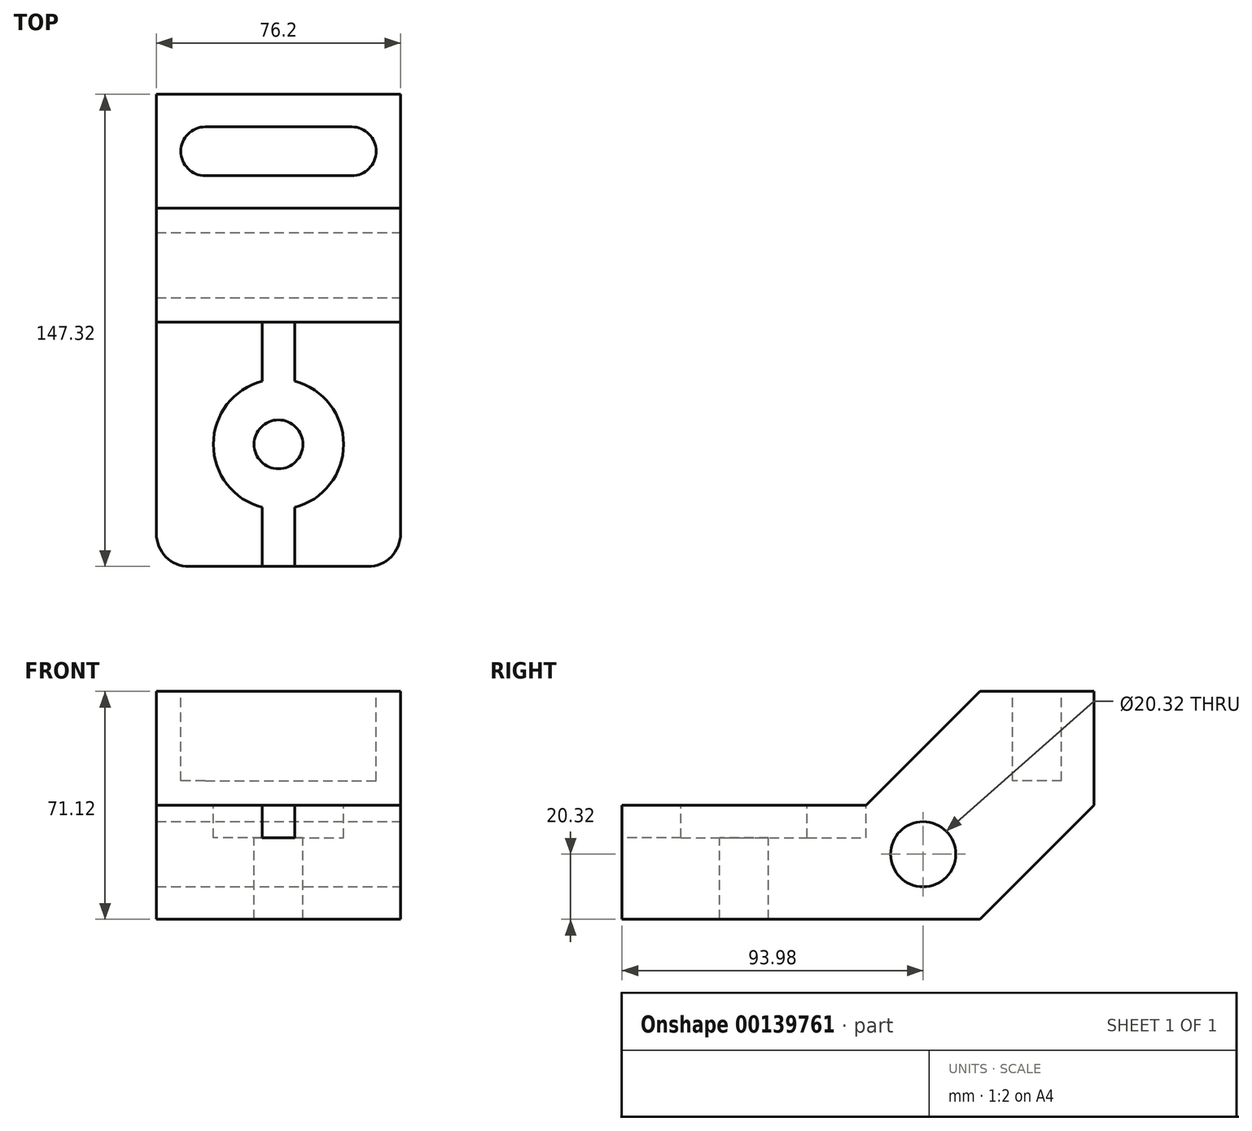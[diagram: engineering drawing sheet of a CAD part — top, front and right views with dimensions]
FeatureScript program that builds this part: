
annotation { "Feature Type Name" : "Feature", "Feature Type Description" : "" }
export const myFeature = defineFeature(function(context is Context, id is Id, definition is map)
    precondition{}
    {
        {
            var Q0;
            Q0=qCreatedBy(makeId("Right.planeOp"),FACE);
            var sketch = newSketch(context, id + "F0", { "sketchPlane" : qUnion([Q0])});
            skLineSegment(sketch, "E0", {"start": v(0, 0) * mm, "end": v(111.76, 0) * mm});
            skLineSegment(sketch, "E1", {"start": v(111.76, 0) * mm, "end": v(147.32, 35.56) * mm});
            skLineSegment(sketch, "E2", {"start": v(147.32, 35.56) * mm, "end": v(147.32, 71.12) * mm});
            skLineSegment(sketch, "E3", {"start": v(147.32, 71.12) * mm, "end": v(111.76, 71.12) * mm});
            skLineSegment(sketch, "E4", {"start": v(111.76, 71.12) * mm, "end": v(76.2, 35.56) * mm});
            skLineSegment(sketch, "E5", {"start": v(76.2, 35.56) * mm, "end": v(0, 35.56) * mm});
            skLineSegment(sketch, "E6", {"start": v(0, 35.56) * mm, "end": v(0, 0) * mm});
            skSolve(sketch);
        }
        {
            var Q0;
            Q0 = qSketchRegion(id + "F0", true);
            extrude(context, id + "F1", {"entities" : qUnion([Q0]), "oppositeDirection" : true, "depth" : 76.2 * mm});
        }
        {
            var Q0;
            Q0=makeQuery(id+"F1.opExtrude","CAP_EDGE",EDGE,{"disambiguationData":[OSD([sQuery(id+"F0.wireOp",EDGE,"E6")])],"isStart":true});
            var Q1;
            Q1=makeQuery(id+"F1.opExtrude","CAP_EDGE",EDGE,{"disambiguationData":[OSD([sQuery(id+"F0.wireOp",EDGE,"E6")])],"isStart":false});
            fillet(context, id + "F2", {"entities" : qUnion([Q0, Q1]), "radius" : 10.16 * mm, "tangentPropagation" : true, "allowEdgeOverflow" : false});
        }
        {
            var Q0;
            Q0=makeQuery(id+"F1.opExtrude","SWEPT_FACE",FACE,{"disambiguationData":[OSD([sQuery(id+"F0.wireOp",EDGE,"E3")])]});
            var sketch = newSketch(context, id + "F3", { "sketchPlane" : qUnion([Q0])});
            skArc(sketch, "E7", {"start": v(-60.96, 137.16) * mm, "mid": v(-68.58, 129.54) * mm, "end": v(-60.96, 121.92) * mm});
            skArc(sketch, "E8", {"start": v(-15.24, 121.92) * mm, "mid": v(-7.62, 129.54) * mm, "end": v(-15.24, 137.16) * mm});
            skLineSegment(sketch, "E9", {"start": v(-60.96, 137.16) * mm, "end": v(-15.24, 137.16) * mm});
            skLineSegment(sketch, "E10", {"start": v(-15.24, 121.92) * mm, "end": v(-60.96, 121.92) * mm});
            skSolve(sketch);
        }
        {
            var Q0;
            Q0 = qSketchRegion(id + "F3", true);
            extrude(context, id + "F4", {"entities" : qUnion([Q0]), "operationType" : NewBodyOperationType.REMOVE, "oppositeDirection" : true, "depth" : 27.94 * mm});
        }
        {
            var Q0;
            Q0=makeQuery(id+"F1.opExtrude","CAP_FACE",FACE,{"disambiguationData":[OSD([sQuery(id+"F0.wireOp",EDGE,"E0"),sQuery(id+"F0.wireOp",EDGE,"E1"),sQuery(id+"F0.wireOp",EDGE,"E2"),sQuery(id+"F0.wireOp",EDGE,"E3"),sQuery(id+"F0.wireOp",EDGE,"E4"),sQuery(id+"F0.wireOp",EDGE,"E5"),sQuery(id+"F0.wireOp",EDGE,"E6")])],"isStart":true});
            var sketch = newSketch(context, id + "F5", { "sketchPlane" : qUnion([Q0])});
            skCircle(sketch, "E11", {"center": v(93.98, 20.32) * mm, "radius": 10.16 * mm});
            skSolve(sketch);
        }
        {
            var Q0;
            Q0 = qSketchRegion(id + "F5", true);
            extrude(context, id + "F6", {"entities" : qUnion([Q0]), "operationType" : NewBodyOperationType.REMOVE, "endBound" : BoundingType.THROUGH_ALL, "oppositeDirection" : true, "depth" : 25.4 * mm});
        }
        {
            var Q0;
            Q0=makeQuery(id+"F1.opExtrude","SWEPT_FACE",FACE,{"disambiguationData":[OSD([sQuery(id+"F0.wireOp",EDGE,"E5")])]});
            var sketch = newSketch(context, id + "F7", { "sketchPlane" : qUnion([Q0])});
            skPoint(sketch, "E12", {"position": v(-38.1, 38.1) * mm});
            skSolve(sketch);
        }
        {
            var Q0;
            Q0=sQuery(id+"F7.wireOp",VERTEX,"E12");
            var Q1;
            Q1=makeQuery(id+"F1.opExtrude","SWEPT_BODY",BODY,{"disambiguationData":[OSD([sQuery(id+"F0.wireOp",EDGE,"E0"),sQuery(id+"F0.wireOp",EDGE,"E1"),sQuery(id+"F0.wireOp",EDGE,"E2"),sQuery(id+"F0.wireOp",EDGE,"E3"),sQuery(id+"F0.wireOp",EDGE,"E4"),sQuery(id+"F0.wireOp",EDGE,"E5"),sQuery(id+"F0.wireOp",EDGE,"E6")])]});
            hole(context, id + "F8", {"style" : HoleStyle.C_BORE, "endStyle" : HoleEndStyle.THROUGH, "holeDiameter" : 15.24 * mm, "cBoreDiameter" : 40.64 * mm, "cBoreDepth" : 10.16 * mm, "locations" : qUnion([Q0]), "scope" : qUnion([Q1]), "isTappedThrough" : true});
        }
        {
            var Q0;
            Q0=makeQuery(id+"F1.opExtrude","SWEPT_FACE",FACE,{"disambiguationData":[OSD([sQuery(id+"F0.wireOp",EDGE,"E5")])]});
            var sketch = newSketch(context, id + "F9", { "sketchPlane" : qUnion([Q0])});
            skLineSegment(sketch, "E13", {"start": v(-33.02, 0) * mm, "end": v(-33.02, 76.2) * mm});
            skLineSegment(sketch, "E14", {"start": v(-33.02, 76.2) * mm, "end": v(-43.18, 76.2) * mm});
            skLineSegment(sketch, "E15", {"start": v(-43.18, 76.2) * mm, "end": v(-43.18, 0) * mm});
            skLineSegment(sketch, "E16", {"start": v(-43.18, 0) * mm, "end": v(-33.02, 0) * mm});
            skSolve(sketch);
        }
        {
            var Q0;
            Q0 = qSketchRegion(id + "F9", true);
            extrude(context, id + "F10", {"entities" : qUnion([Q0]), "operationType" : NewBodyOperationType.REMOVE, "oppositeDirection" : true, "depth" : 10.16 * mm});
        }
    });
